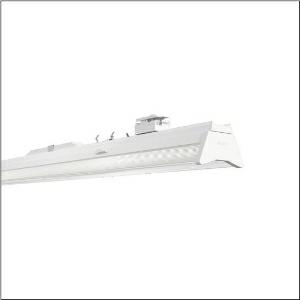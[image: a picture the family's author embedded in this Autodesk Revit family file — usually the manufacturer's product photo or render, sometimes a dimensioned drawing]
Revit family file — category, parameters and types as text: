
# Revit family: licross_11_performance_tw_51tm16tnt85x
name_source: partatom
category: Lighting Fixtures
units: mm (PartAtom-declared; Revit-internal decimal feet)

## family parameters
Cut with Voids When Loaded = No
Host = Face
Light Source = No
Part Type = Normal
Room Calculation Point = No
Round Connector Dimension = Use Diameter
Shared = No

## types (1)
- --- (1 x LED 2700 K ... 6500 K, 8930 lm, 56 W, 2700K)
    Apparent Load = 56 VA
    CIE Flux Codes = 63 87 95 78 100
    Color Rendering = 80
    Color Temperature = 2700K
    Default Elevation = 1800 mm
    Description = Licross 11 Performance TW, luminaire insert, of sheet steel, galvanised, coil coated, white, length: 1.500mm, width: 120mm, height: 123mm, LED rated luminous flux: 8.930lm, light colour: 8tw, SDCM (Standard Deviation of Colour Matching)MacAdam ≤ 2 SDCM (initial), control gear: DALI DT8, with plug, 5-pole, with phase selection, mains connection: 220..240V, AC, 50/60Hz, rated input power: 56W, internal wiring halogen-free, primary light control with lens, of plastic, primary optical cover: cover, of PMMA, light emission: direct/indirect distribution, primary light characteristic: symmetric, protection rating (complete): IP40, insulation class (complete): insulation class I (protective earthing), certification: CE, ENEC, VDE, UKCA, protection symbol: D if used in an environment without relevant dust loads with corresponding accessories, impact resistance: IK06, permissible ambient temperature for indoor applications: -25..+35°C, corresponds to IFS (International Featured Standards) requirements for safety and quality in the food industry, reducing of maximum allowable ambient temperature of 5°C with ceiling mounting, LABS conformity tested according to VDMA 24364:2018-05, The light source and the operating device comply with the requirements of the Ecodesign Regulation (EU) 2019/2020 and are replaceable in accordance with this regulation, packaging unit: 1 piece
    Height = 114 mm
    Lamp = 1 x LED 2700 K ... 6500 K
    Lamp Light Flux = 8930 lm
    Lamp Power = 56 W
    Lamp count = 1
    Length = 1500 mm
    Luminous efficacy = 159 lm/W
    Manufacturer = Siteco
    ModVariant = No
    Model = 51TM16TNT85X
    Mounting Place = Ceiling
    Mounting Type = Pendant
    Number of Poles = 1
    OnlyDefault = Yes
    Power Factor = 1
    Product Name = Licross 11 Performance TW
    Product group = luminaire insert | ceiling pendant
    ProductGroupID = 901
    Protection Class = Protection class I
    Protection Degree = IP 40
    RLX_Detail_Level = 1
    RLX_Emergency_Light_Flux = 0 lm
    RLX_Emergency_Type = 0
    RLX_Emergency_Type_DB = No
    RlxData = <blob elided: 30657 chars, md5=ce38fe9d>
    Socket = socket
    Standby Power = 0 W
    System Light Flux = 8930 lm
    System Power = 56 W
    Type Comments = individual setting: CCT=2700K
    Type Image = l_1256138.jpg
    URL = http://relux.com
    VarID = @adj_056361
    Voltage = 0 V
    Weight = 0.00 kg
    Width = 120 mm

## geometry (parser evidence)
native form markers: Blend x4, Sweep x11
no freeform markers — native parametric forms only
